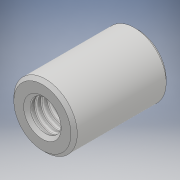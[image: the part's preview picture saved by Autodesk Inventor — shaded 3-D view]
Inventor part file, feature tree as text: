
AUTODESK INVENTOR PART (.ipt)
format: ipt  version: 2018 (Build 220112000, 112)  size: 115,200 bytes
history: native  units: mm
features: extrude x1, hole x1, chamfer x1, sketch x1
ambient origin geometry x8: Origin, YZ Plane, XZ Plane, XY Plane, X Axis, Y Axis, Z Axis, Center Point
bodies: Solid1 (feature_tree)
feature tree (4):
  extrude  "Extrusion1"  Depth=15.0mm TaperAngle=0.0deg
  hole  "Hole1"  [1 undecoded]
  chamfer  "Chamfer1"  [1 undecoded]
  sketch  "Sketch1"  dims[d0=10.0mm d1=15.0mm d2=0.0mm d12=10.0mm d13=10.0mm d5=4.917mm d6=12.0mm d7=4.0mm d8=2.0mm d9=90.0deg d10=17.1mm d11=20.594885mm d14=0.5mm d15=2.0mm d16=45.0deg]
note: 2 required parameter values undecoded (feature->parameter linkage not recoverable at this tier; creation-order binding heuristic only, values carry confidence <= 0.55)
